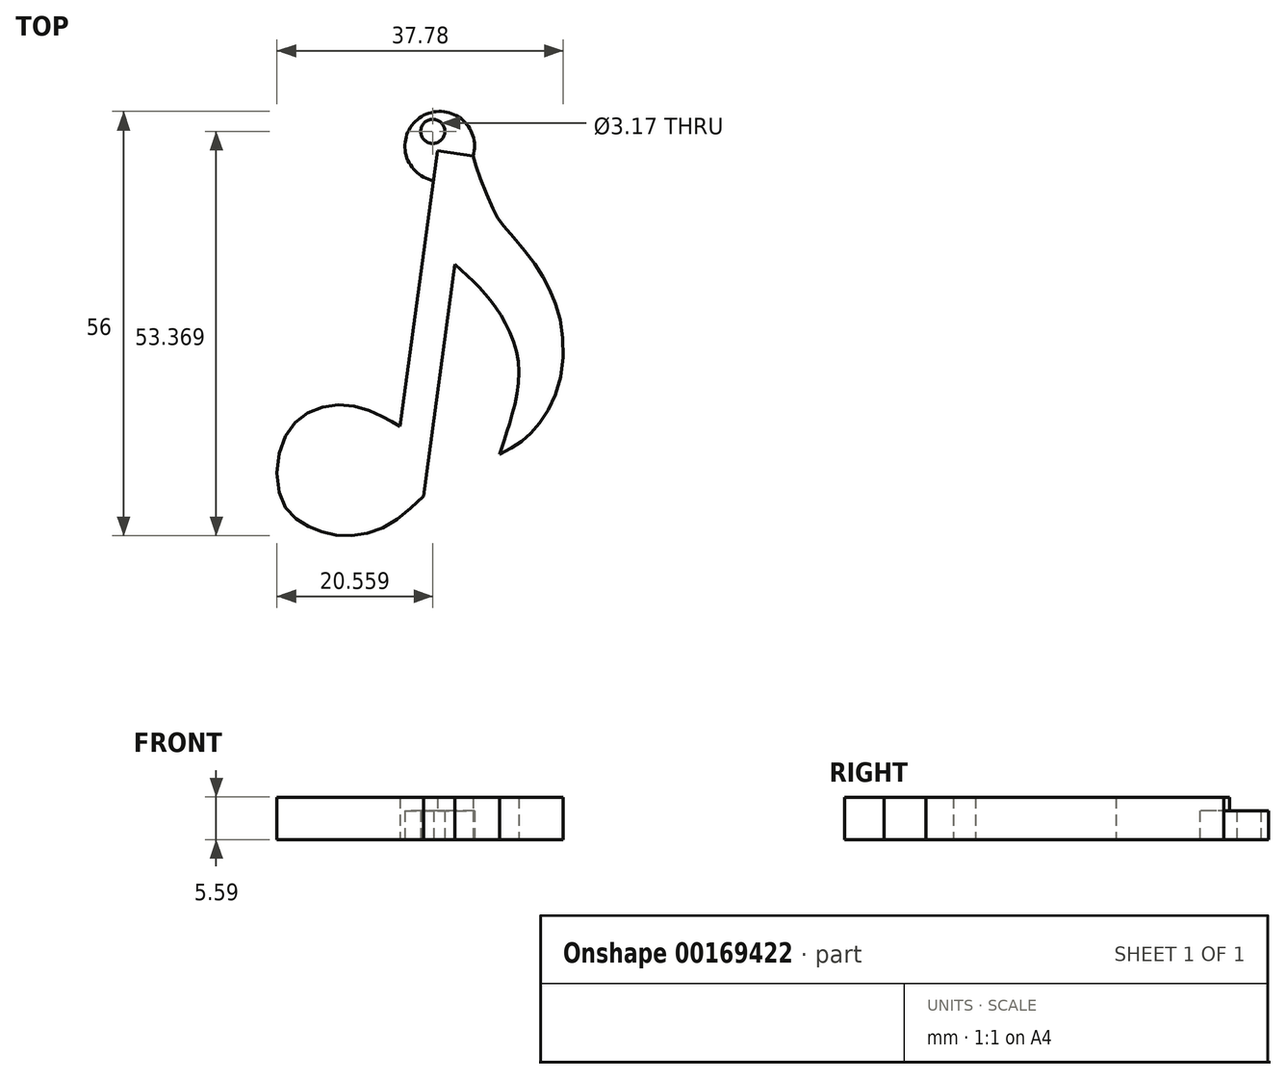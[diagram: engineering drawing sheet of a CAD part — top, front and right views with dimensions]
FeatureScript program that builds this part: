
annotation { "Feature Type Name" : "Feature", "Feature Type Description" : "" }
export const myFeature = defineFeature(function(context is Context, id is Id, definition is map)
    precondition{}
    {
        {
            var Q0;
            Q0=qCreatedBy(makeId("Top.planeOp"),FACE);
            var sketch = newSketch(context, id + "F0", { "sketchPlane" : qUnion([Q0])});
            skLineSegment(sketch, "E0", {"start": v(1.17, 17.26) * mm, "end": v(-3.77, -19.15) * mm});
            skFitSpline(sketch, "E1", {"points": [v(-3.77, -19.15) * mm, v(-5.73, -18.04) * mm, v(-10.07, -16.42) * mm, v(-15.52, -17.1) * mm, v(-19.35, -21.36) * mm, v(-19.35, -29.02) * mm, v(-15.77, -32.35) * mm, v(-11.35, -33.54) * mm, v(-5.81, -32.43) * mm, v(-0.7, -28.34) * mm], "startDerivative": vector(-23.95, 14.17) * mm, "endDerivative": vector(38.59, 37.7) * mm});
            skLineSegment(sketch, "E2", {"start": v(-0.7, -28.34) * mm, "end": v(3.45, 2.29) * mm});
            skFitSpline(sketch, "E3", {"points": [v(3.45, 2.29) * mm, v(6.87, -1.01) * mm, v(9.94, -5.18) * mm, v(11.9, -11.57) * mm, v(10.7, -18.64) * mm, v(9.34, -22.8) * mm], "startDerivative": vector(19, -17.31) * mm, "endDerivative": vector(-7.45, -21.7) * mm});
            skFitSpline(sketch, "E4", {"points": [v(9.34, -22.8) * mm, v(12.3, -21.05) * mm, v(14.7, -18.62) * mm, v(17.27, -13.28) * mm, v(17.46, -5.69) * mm, v(15.75, -0.68) * mm, v(13.17, 3.45) * mm, v(9.78, 7.5) * mm, v(8.66, 9.18) * mm, v(6.69, 13.96) * mm, v(5.85, 16.54) * mm], "startDerivative": vector(35.18, 18.8) * mm, "endDerivative": vector(-8.54, 28.72) * mm});
            skLineSegment(sketch, "E5", {"start": v(1.17, 17.26) * mm, "end": v(5.85, 16.54) * mm});
            skArc(sketch, "E6", {"start": v(5.85, 16.54) * mm, "mid": v(-0.96, 21.75) * mm, "end": v(0.63, 13.32) * mm});
            skCircle(sketch, "E7", {"center": v(0.53, 19.8) * mm, "radius": 1.59 * mm});
            skSolve(sketch);
        }
        {
            var Q0;
            {var subQ0=sQuery(id+"F0.wireOp",EDGE,"E1");Q0=makeQuery(id+"F0.imprint","IMPRINT",FACE,{"disambiguationData":[TD([[makeQuery(id+"F0.imprint","IMPRINT",EDGE,{"derivedFrom":subQ0}),1.0]])]});}
            extrude(context, id + "F1", {"entities" : qUnion([Q0]), "depth" : 5.6 * mm});
        }
        {
            var Q0;
            {var subQ0=sQuery(id+"F0.wireOp",EDGE,"E5");Q0=makeQuery(id+"F0.imprint","IMPRINT",FACE,{"disambiguationData":[TD([[makeQuery(id+"F0.imprint","IMPRINT",EDGE,{"derivedFrom":subQ0}),1.0]])]});}
            extrude(context, id + "F2", {"entities" : qUnion([Q0]), "operationType" : NewBodyOperationType.ADD, "depth" : 3.8 * mm});
        }
    });
